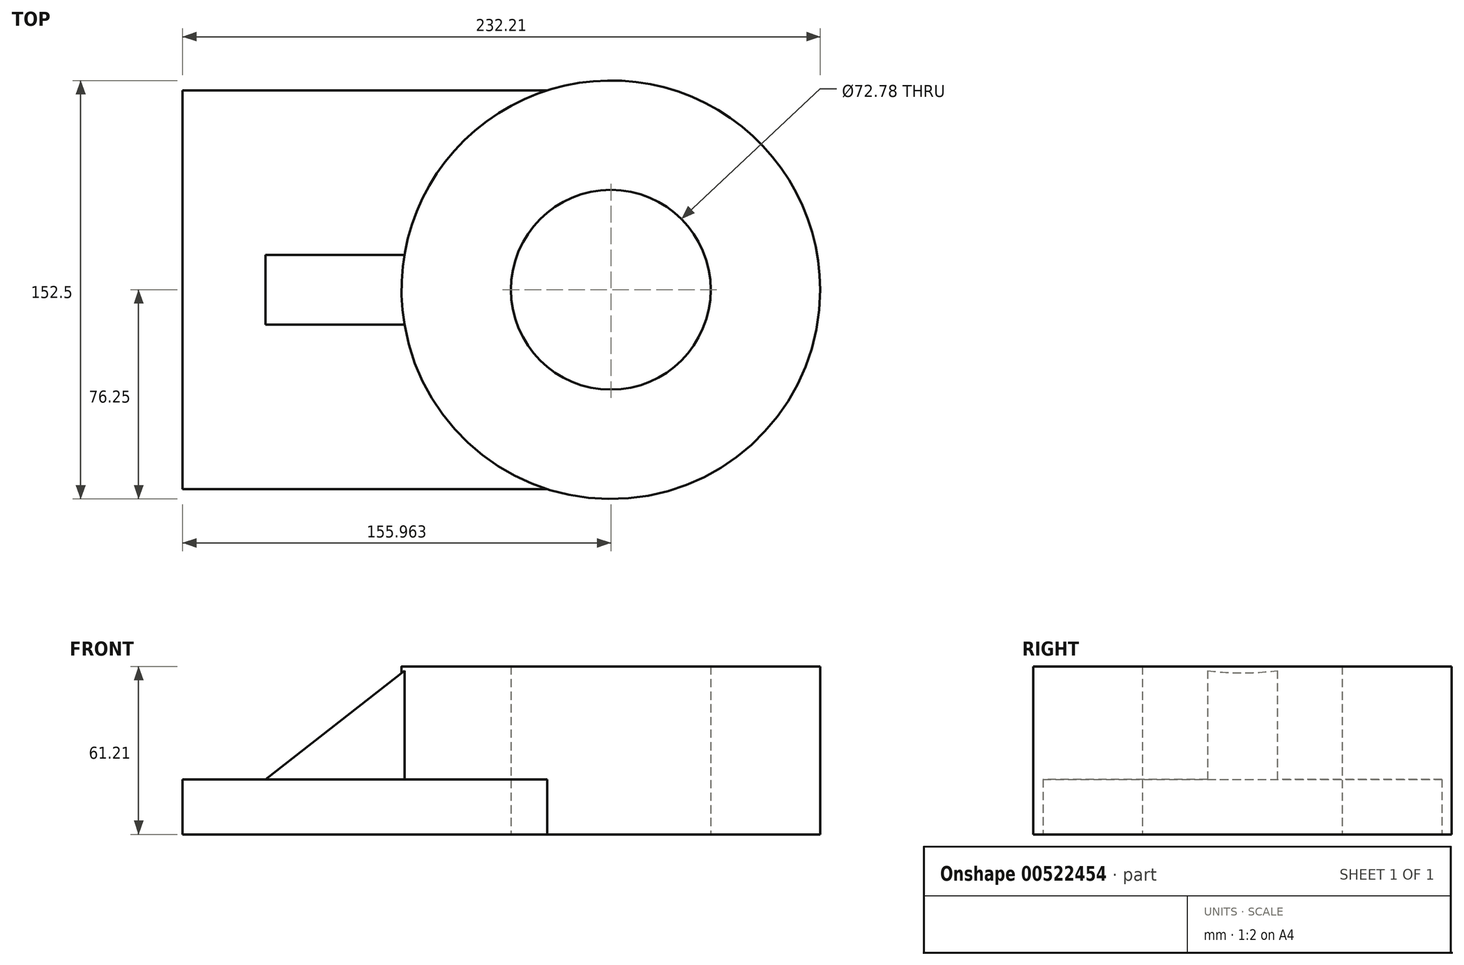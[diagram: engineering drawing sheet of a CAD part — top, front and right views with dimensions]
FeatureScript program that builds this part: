
annotation { "Feature Type Name" : "Feature", "Feature Type Description" : "" }
export const myFeature = defineFeature(function(context is Context, id is Id, definition is map)
    precondition{}
    {
        {
            var Q0;
            Q0=qCreatedBy(makeId("Top.planeOp"),FACE);
            var sketch = newSketch(context, id + "F0", { "sketchPlane" : qUnion([Q0])});
            skLineSegment(sketch, "E0.bottom", {"start": v(64.2, -72.65) * mm, "end": v(-70.86, -72.65) * mm});
            skLineSegment(sketch, "E0.top", {"start": v(64.2, 72.65) * mm, "end": v(-70.86, 72.65) * mm});
            skLineSegment(sketch, "E0.right", {"start": v(-70.86, -72.65) * mm, "end": v(-70.86, 72.65) * mm});
            skPoint(sketch, "E0.middle", {"position": v(0, 0) * mm});
            skCircle(sketch, "E1", {"center": v(107.5, 0) * mm, "radius": 46.97 * mm});
            skCircle(sketch, "E2", {"center": v(107.5, 0) * mm, "radius": 84.57 * mm});
            skPoint(sketch, "E3.orphan", {"position": v(70.86, 72.65) * mm});
            skPoint(sketch, "E4.orphan", {"position": v(70.86, -72.65) * mm});
            skSolve(sketch);
        }
        {
            var Q0;
            {var subQ0=sQuery(id+"F0.wireOp",EDGE,"E0.bottom");Q0=makeQuery(id+"F0.imprint","IMPRINT",FACE,{"disambiguationData":[TD([[makeQuery(id+"F0.imprint","IMPRINT",EDGE,{"derivedFrom":subQ0}),-1.0]])]});}
            extrude(context, id + "F1", {"entities" : qUnion([Q0]), "depth" : 20.07 * mm, "offsetDistance" : 25.4 * mm});
        }
        {
            var Q0;
            Q0=qCreatedBy(makeId("Top.planeOp"),FACE);
            var sketch = newSketch(context, id + "F2", { "sketchPlane" : qUnion([Q0])});
            skCircle(sketch, "E5", {"center": v(85.1, 0) * mm, "radius": 36.39 * mm});
            skCircle(sketch, "E6", {"center": v(85.1, 0) * mm, "radius": 76.25 * mm});
            skSolve(sketch);
        }
        {
            var Q0;
            Q0 = qSketchRegion(id + "F2", true);
            extrude(context, id + "F3", {"entities" : qUnion([Q0]), "operationType" : NewBodyOperationType.ADD, "depth" : 61.2 * mm, "offsetDistance" : 25.4 * mm});
        }
        {
            var Q0;
            Q0=qCreatedBy(makeId("Front.planeOp"),FACE);
            var sketch = newSketch(context, id + "F4", { "sketchPlane" : qUnion([Q0])});
            skLineSegment(sketch, "E7", {"start": v(10.08, 59.8) * mm, "end": v(-42.62, 18.56) * mm});
            skLineSegment(sketch, "E8", {"start": v(-42.62, 18.56) * mm, "end": v(11, 18.56) * mm});
            skLineSegment(sketch, "E9", {"start": v(11, 18.56) * mm, "end": v(10.08, 59.8) * mm});
            skSolve(sketch);
        }
        {
            var Q0;
            Q0 = qSketchRegion(id + "F4", true);
            extrude(context, id + "F5", {"entities" : qUnion([Q0]), "operationType" : NewBodyOperationType.ADD, "endBound" : BoundingType.SYMMETRIC, "depth" : 25.4 * mm, "offsetDistance" : 25.4 * mm});
        }
    });
